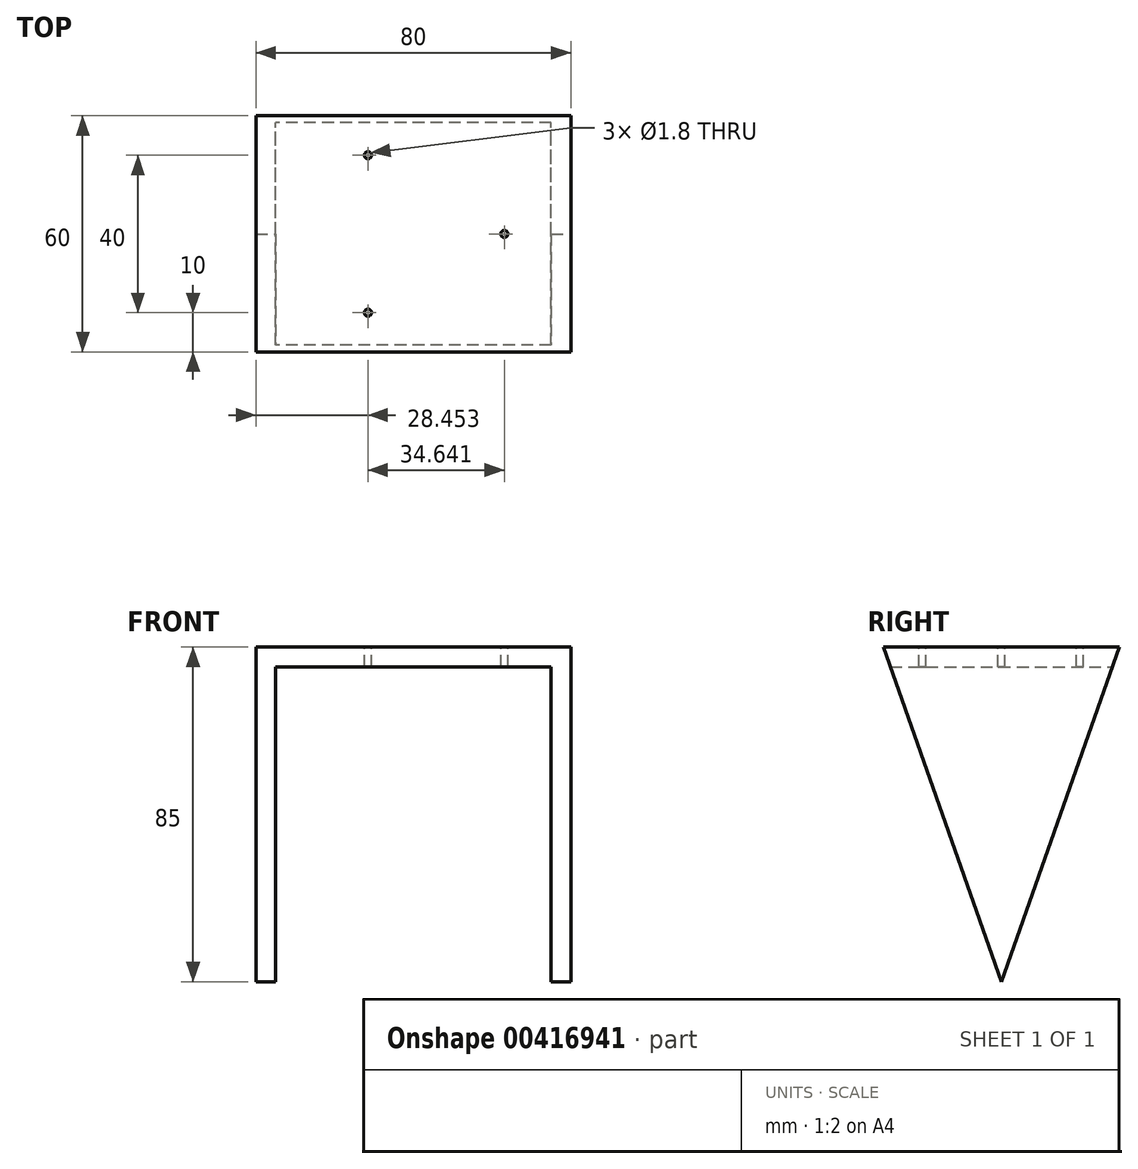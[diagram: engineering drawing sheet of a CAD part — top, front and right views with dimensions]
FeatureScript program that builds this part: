
annotation { "Feature Type Name" : "Feature", "Feature Type Description" : "" }
export const myFeature = defineFeature(function(context is Context, id is Id, definition is map)
    precondition{}
    {
        {
            var Q0;
            Q0=qCreatedBy(makeId("Front.planeOp"),FACE);
            var sketch = newSketch(context, id + "F0", { "sketchPlane" : qUnion([Q0])});
            skLineSegment(sketch, "E0.bottom", {"start": v(40, -42.5) * mm, "end": v(-40, -42.5) * mm});
            skLineSegment(sketch, "E0.top", {"start": v(40, 42.5) * mm, "end": v(-40, 42.5) * mm});
            skLineSegment(sketch, "E0.left", {"start": v(40, -42.5) * mm, "end": v(40, 42.5) * mm});
            skLineSegment(sketch, "E0.right", {"start": v(-40, -42.5) * mm, "end": v(-40, 42.5) * mm});
            skPoint(sketch, "E0.middle", {"position": v(0, 0) * mm});
            skLineSegment(sketch, "E1", {"start": v(-40, 37.5) * mm, "end": v(40, 37.5) * mm});
            skLineSegment(sketch, "E2", {"start": v(-35, 42.5) * mm, "end": v(-35, -42.5) * mm});
            skLineSegment(sketch, "E3", {"start": v(35, 42.5) * mm, "end": v(35, -42.5) * mm});
            skSolve(sketch);
        }
        {
            var Q0;
            {var subQ0=sQuery(id+"F0.wireOp",EDGE,"E0.right");var subQ1=sQuery(id+"F0.wireOp",EDGE,"E0.bottom");var subQ2=makeQuery(id+"F0.imprint","INTERSECT",VERTEX,{"derivedFrom":[subQ1,subQ0]});Q0=makeQuery(id+"F0.imprint","IMPRINT",FACE,{"disambiguationData":[TD([[makeQuery(id+"F0.imprint","IMPRINT",EDGE,{"disambiguationData":[TD([[subQ2,1.0]])],"derivedFrom":subQ1}),-1.0]])]});}
            var Q1;
            {var subQ0=sQuery(id+"F0.wireOp",EDGE,"E0.right");var subQ1=sQuery(id+"F0.wireOp",EDGE,"E0.top");var subQ2=makeQuery(id+"F0.imprint","INTERSECT",VERTEX,{"derivedFrom":[subQ1,subQ0]});Q1=makeQuery(id+"F0.imprint","IMPRINT",FACE,{"disambiguationData":[TD([[makeQuery(id+"F0.imprint","IMPRINT",EDGE,{"disambiguationData":[TD([[subQ2,1.0]])],"derivedFrom":subQ1}),1.0]])]});}
            var Q2;
            {var subQ0=sQuery(id+"F0.wireOp",EDGE,"E2");var subQ1=sQuery(id+"F0.wireOp",EDGE,"E0.top");var subQ2=makeQuery(id+"F0.imprint","INTERSECT",VERTEX,{"derivedFrom":[subQ1,subQ0]});Q2=makeQuery(id+"F0.imprint","IMPRINT",FACE,{"disambiguationData":[TD([[makeQuery(id+"F0.imprint","IMPRINT",EDGE,{"disambiguationData":[TD([[subQ2,1.0]])],"derivedFrom":subQ1}),1.0]])]});}
            var Q3;
            {var subQ0=sQuery(id+"F0.wireOp",EDGE,"E0.left");var subQ1=sQuery(id+"F0.wireOp",EDGE,"E0.top");var subQ2=makeQuery(id+"F0.imprint","INTERSECT",VERTEX,{"derivedFrom":[subQ1,subQ0]});Q3=makeQuery(id+"F0.imprint","IMPRINT",FACE,{"disambiguationData":[TD([[makeQuery(id+"F0.imprint","IMPRINT",EDGE,{"disambiguationData":[TD([[subQ2,-1.0]])],"derivedFrom":subQ1}),1.0]])]});}
            var Q4;
            {var subQ0=sQuery(id+"F0.wireOp",EDGE,"E0.left");var subQ1=sQuery(id+"F0.wireOp",EDGE,"E0.bottom");var subQ2=makeQuery(id+"F0.imprint","INTERSECT",VERTEX,{"derivedFrom":[subQ1,subQ0]});Q4=makeQuery(id+"F0.imprint","IMPRINT",FACE,{"disambiguationData":[TD([[makeQuery(id+"F0.imprint","IMPRINT",EDGE,{"disambiguationData":[TD([[subQ2,-1.0]])],"derivedFrom":subQ1}),-1.0]])]});}
            extrude(context, id + "F1", {"entities" : qUnion([Q0, Q1, Q2, Q3, Q4]), "depth" : 60 * mm});
        }
        {
            var Q0;
            Q0=makeQuery(id+"F1.opExtrude","SWEPT_FACE",FACE,{"disambiguationData":[OSD([sQuery(id+"F0.wireOp",EDGE,"E0.top")])]});
            var sketch = newSketch(context, id + "F2", { "sketchPlane" : qUnion([Q0])});
            skPoint(sketch, "E4", {"position": v(0, -30) * mm});
            skPoint(sketch, "E4.positionSnap0", {"position": v(0, 0) * mm});
            skCircle(sketch, "E5.cCircle", {"center": v(0, -30) * mm, "radius": 11.55 * mm, "construction": true});
            skLineSegment(sketch, "E5.0", {"start": v(23.1, -30) * mm, "end": v(-11.55, -50) * mm});
            skLineSegment(sketch, "E5.1", {"start": v(-11.55, -50) * mm, "end": v(-11.55, -10) * mm});
            skLineSegment(sketch, "E5.2", {"start": v(-11.55, -10) * mm, "end": v(23.1, -30) * mm});
            skPoint(sketch, "E5.0.midPoint", {"position": v(5.77, -40) * mm});
            skPoint(sketch, "E6", {"position": v(23.1, -30) * mm});
            skCircle(sketch, "E7", {"center": v(23.1, -30) * mm, "radius": 0.9 * mm});
            skPoint(sketch, "E8", {"position": v(-11.55, -10) * mm});
            skPoint(sketch, "E9", {"position": v(-11.55, -50) * mm});
            skCircle(sketch, "E10", {"center": v(-11.55, -10) * mm, "radius": 0.9 * mm});
            skCircle(sketch, "E11", {"center": v(-11.55, -50) * mm, "radius": 0.9 * mm});
            skSolve(sketch);
        }
        {
            var Q0;
            {var subQ0=sQuery(id+"F2.wireOp",EDGE,"E5.2");var subQ1=sQuery(id+"F2.wireOp",EDGE,"E5.0");var subQ2=makeQuery(id+"F2.imprint","INTERSECT",VERTEX,{"derivedFrom":[subQ1,subQ0]});Q0=makeQuery(id+"F2.imprint","IMPRINT",FACE,{"disambiguationData":[TD([[makeQuery(id+"F2.imprint","IMPRINT",EDGE,{"disambiguationData":[TD([[subQ2,-1.0]])],"derivedFrom":subQ1}),1.0]])]});}
            var Q1;
            {var subQ0=sQuery(id+"F2.wireOp",EDGE,"E5.2");var subQ1=sQuery(id+"F2.wireOp",EDGE,"E5.0");var subQ2=makeQuery(id+"F2.imprint","INTERSECT",VERTEX,{"derivedFrom":[subQ1,subQ0]});Q1=makeQuery(id+"F2.imprint","IMPRINT",FACE,{"disambiguationData":[TD([[makeQuery(id+"F2.imprint","IMPRINT",EDGE,{"disambiguationData":[TD([[subQ2,-1.0]])],"derivedFrom":subQ1}),-1.0]])]});}
            var Q2;
            {var subQ0=sQuery(id+"F2.wireOp",EDGE,"E5.2");var subQ1=sQuery(id+"F2.wireOp",EDGE,"E5.1");var subQ2=makeQuery(id+"F2.imprint","INTERSECT",VERTEX,{"derivedFrom":[subQ1,subQ0]});Q2=makeQuery(id+"F2.imprint","IMPRINT",FACE,{"disambiguationData":[TD([[makeQuery(id+"F2.imprint","IMPRINT",EDGE,{"disambiguationData":[TD([[subQ2,1.0]])],"derivedFrom":subQ1}),-1.0]])]});}
            var Q3;
            {var subQ0=sQuery(id+"F2.wireOp",EDGE,"E5.2");var subQ1=sQuery(id+"F2.wireOp",EDGE,"E5.1");var subQ2=makeQuery(id+"F2.imprint","INTERSECT",VERTEX,{"derivedFrom":[subQ1,subQ0]});Q3=makeQuery(id+"F2.imprint","IMPRINT",FACE,{"disambiguationData":[TD([[makeQuery(id+"F2.imprint","IMPRINT",EDGE,{"disambiguationData":[TD([[subQ2,1.0]])],"derivedFrom":subQ1}),1.0]])]});}
            var Q4;
            {var subQ0=sQuery(id+"F2.wireOp",EDGE,"E5.1");var subQ1=sQuery(id+"F2.wireOp",EDGE,"E5.0");var subQ2=makeQuery(id+"F2.imprint","INTERSECT",VERTEX,{"derivedFrom":[subQ1,subQ0]});Q4=makeQuery(id+"F2.imprint","IMPRINT",FACE,{"disambiguationData":[TD([[makeQuery(id+"F2.imprint","IMPRINT",EDGE,{"disambiguationData":[TD([[subQ2,1.0]])],"derivedFrom":subQ1}),-1.0]])]});}
            var Q5;
            {var subQ0=sQuery(id+"F2.wireOp",EDGE,"E5.1");var subQ1=sQuery(id+"F2.wireOp",EDGE,"E5.0");var subQ2=makeQuery(id+"F2.imprint","INTERSECT",VERTEX,{"derivedFrom":[subQ1,subQ0]});Q5=makeQuery(id+"F2.imprint","IMPRINT",FACE,{"disambiguationData":[TD([[makeQuery(id+"F2.imprint","IMPRINT",EDGE,{"disambiguationData":[TD([[subQ2,1.0]])],"derivedFrom":subQ1}),1.0]])]});}
            extrude(context, id + "F3", {"entities" : qUnion([Q0, Q1, Q2, Q3, Q4, Q5]), "operationType" : NewBodyOperationType.REMOVE, "endBound" : BoundingType.THROUGH_ALL, "oppositeDirection" : true, "depth" : 25 * mm});
        }
        {
            var Q0;
            Q0=makeQuery(id+"F1.opExtrude","SWEPT_FACE",FACE,{"disambiguationData":[OSD([sQuery(id+"F0.wireOp",EDGE,"E0.left")])]});
            var sketch = newSketch(context, id + "F4", { "sketchPlane" : qUnion([Q0])});
            skPoint(sketch, "E12", {"position": v(-30, -42.5) * mm});
            skLineSegment(sketch, "E13", {"start": v(-30, -42.5) * mm, "end": v(0, 42.5) * mm});
            skLineSegment(sketch, "E14", {"start": v(-30, -42.5) * mm, "end": v(-60, 42.5) * mm});
            skSolve(sketch);
        }
        {
            var Q0;
            {var subQ0=sQuery(id+"F4.wireOp",EDGE,"E14");Q0=makeQuery(id+"F4.imprint","IMPRINT",FACE,{"disambiguationData":[TD([[makeQuery(id+"F4.imprint","IMPRINT",EDGE,{"derivedFrom":subQ0}),1.0]])]});}
            var Q1;
            {var subQ0=sQuery(id+"F4.wireOp",EDGE,"E13");Q1=makeQuery(id+"F4.imprint","IMPRINT",FACE,{"disambiguationData":[TD([[makeQuery(id+"F4.imprint","IMPRINT",EDGE,{"derivedFrom":subQ0}),-1.0]])]});}
            extrude(context, id + "F5", {"entities" : qUnion([Q0, Q1]), "operationType" : NewBodyOperationType.REMOVE, "endBound" : BoundingType.THROUGH_ALL, "oppositeDirection" : true, "depth" : 25 * mm});
        }
    });
